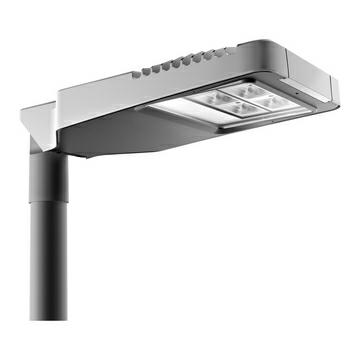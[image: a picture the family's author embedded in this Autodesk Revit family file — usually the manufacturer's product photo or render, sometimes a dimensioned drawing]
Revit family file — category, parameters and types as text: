
# Revit family: Lighting-Stradale-GEWISS-ROAD[5]MINI-LED_OTTICA_WIDE-W_CLII
name_source: partatom
category: Apparecchi per illuminazione
units: mm (PartAtom-declared; Revit-internal decimal feet)

## family parameters
Basato su piano di lavoro = No
Condiviso = No
Punto di calcolo locali = No
Quota connettore circolare = Usa diametro
Sempre verticale = Sì
Sorgente d'illuminazione = No
Taglio con vuoti quando caricato = No
Tipo di parte = Normale

## types (1)
- Lighting-Stradale-GEWISS-ROAD[5]MINI-LED_OTTICA_WIDE-W_CLII
    Alimentatore = Incluso
    Apparecchio a ridotta temperatura superficiale = -
    Applicazione = Esterno
    Cablaggio = Sezionatore
    Caratteristiche elettriche e gestione della luce = -
    Caratteristiche ottiche e illuminotecniche = -
    Carico apparente = 54 VA
    Catalogo = LIGHTING
    Catalogo Serie = ROAD [5]
    Certificazione DIN 18032-3 = -
    Certificazioni e classificazioni = -
    Classe fotobiologica = RG0
    Classe isolamento = II
    Classificazione: = -
    Codice Electrocod = 244C
    Codice digitale univoco (Datamatrix) = Attualmente non presente
    Colore = Grigio grafite
    Commenti sul wattaggio = 54W
    Contesto = Illuminazione stradale e parcheggi
    Controllo abbagliamento e luminanza = G*4 - ULOR = 0
    Corpo = Alluminio pressofuso
    Corrente di pilotaggio. = 0,7A
    Descrizione = GWR5272BW - ROAD5 MINI WIDE 2M 4000K 0,7A CL2 BIR.W
    Dispositivo di protezione = DM 10KV / CM 10KV
    Distanza minima dall'oggetto illuminato = 1M
    Durata di vita = L90B10 (Tq+25°C) = 100.000 h
    Efficienza luminosa (lm/W) = 108
    Finitura colore = Verniciato a polveri
    Fissaggio = Testa palo - Sbraccio
    Frequenza nominale (Hz) = 50 / 60
    Gancio di chiusura = Maniglia frontale integrata
    Garanzia = 5 anni
    Grado di protezione = IP66
    Gruppo ottico = Riflettore in PC metallizzato
    Guarnizioni = silicone antinvecchiamento
    IDF = f5e8a357-a8c2-401f-901a-a866161b1b8a
    IDT = 7b37660f6c27427dab2b33d7b45cf4bf
    IPEA = STRADALE = A++ // GRANDI AREE = A4+ // CICLOPEDONALI = A+ // AREE VERDI = A+ // CENTRO STORICO = A5+
    Immagine tipo = GWR5276M.jpg
    Inclinazione = -20° ÷ +10° sbraccio - -10° ÷ +20° testa palo
    Indice di resa cromatica = CRI-70
    Informazioni generali = -
    Installazione e manutenzione = -
    LED Life time (L80B10) = 100000H
    Lampada: = LED
    Lumen output (lm) = 10800
    Materiali = -
    Modello = GWR5272BW
    Norma di riferimento = EN 60598-2-3, EN 60598-1 IEC/TR 62778
    Numero moduli = 2 (2x3 LED)
    Ottica = WIDE
    Peso (kg): = 6,59999999999999
    Potenza assorbita : = 100 W @ 0.7A
    Potenza di sistema = 100W
    Produttore = GEWISS S.p.A.
    Regolazione inclinazione = -20° ÷ +10° sbraccio - -10° ÷ +20° testa palo
    Resistenza agli urti = IK08
    Resistenza al filo incandescente = -
    Resistenza alle sovratensioni = 10 KV in modalità comune
    SEO = Stradale
    Scheda Tecnica = https://www.gewiss.com
    Schermo = Vetro piano temperato spessore 4mm
    Sistema di controllo = Biregime con autoapprendimento
    Sostituibilità gruppo ottico = Non disponibile
    Sostituibilità piastra di cablaggio = Non disponibile
    Superficie massima esposta al vento = 0,149999999999999M2
    Superficie massima esposta al vento : = 0,15 m²
    Temperatura di colore = 4000K
    Temperatura di colore: = 4000 K (CRI>70)
    Temperatura di esercizio = -25 +30 °C
    Temperatura di stoccaggio = -
    Temperatura di utilizzo = -25 +30 °C
    Tensione = 220/240 V - 50/60 Hz
    Tensione di alimentazione = 220 - 240 V
    Tipo alimentatore = Driver Led in corrente continua
    Tipo di apparecchio = Apparecchiatura stradale a LED
    Tipo di installazione e montaggio = Testa palo - Sbraccio
    Tipologia = Biregime
    Tipologia sorgente luminosa = LED - Non sostituibile
    Tolleranza cromatica = SDCM = 5
    URL = https://www.gewiss.com
    Vano di alimentazione = Integrato
    Versione file RFA = 20.11
    Viti esterne = Acciaio inox

## geometry (parser evidence)
native form markers: Blend x2
no freeform markers — native parametric forms only
